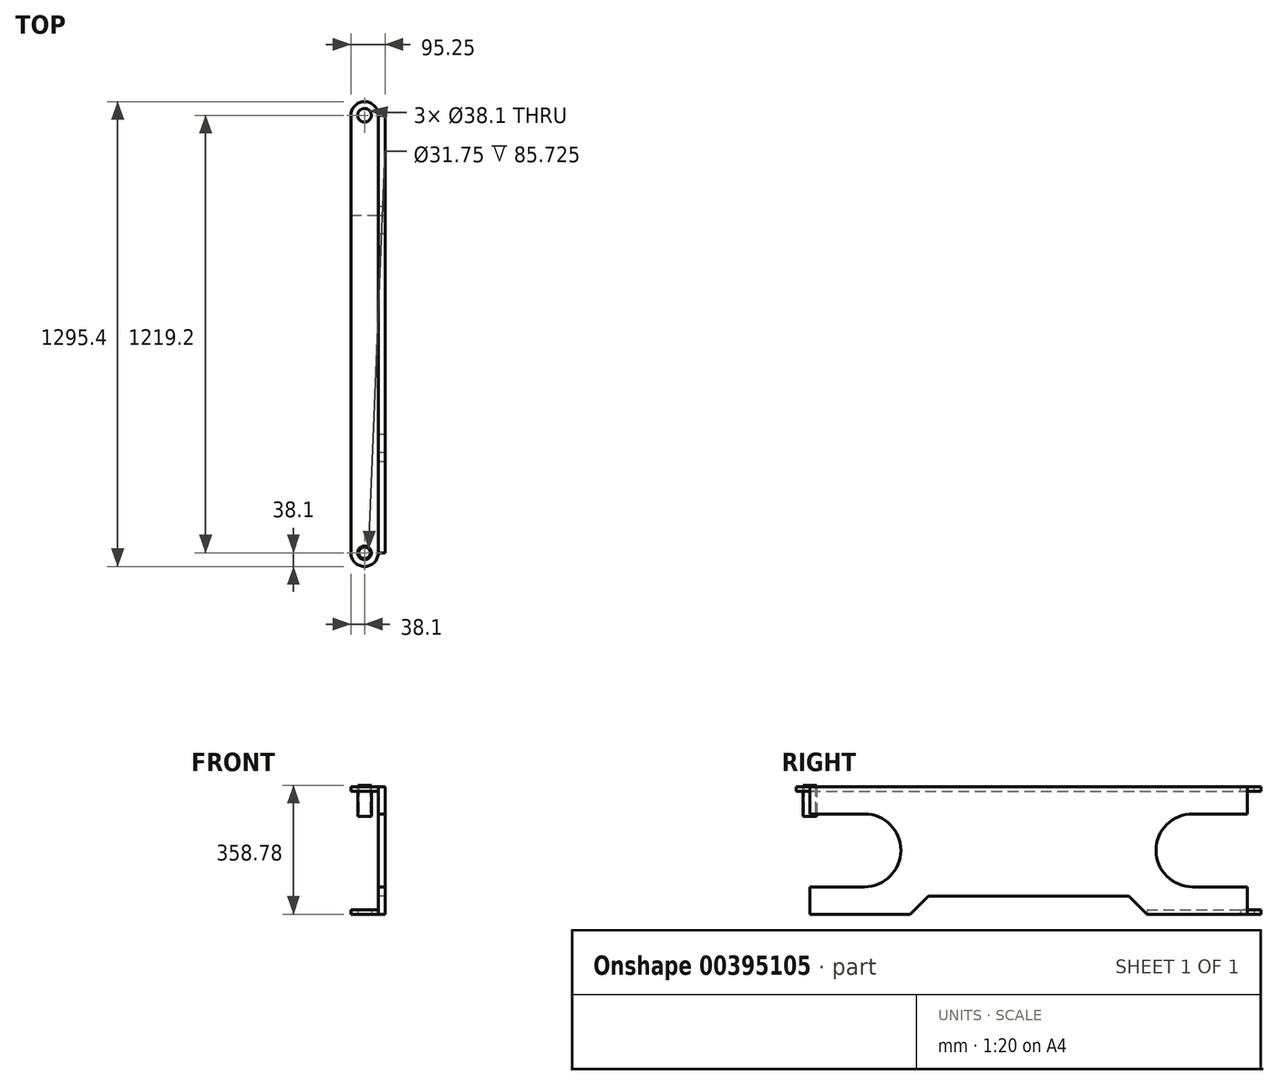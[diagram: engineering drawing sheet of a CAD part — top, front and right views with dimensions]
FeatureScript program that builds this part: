
annotation { "Feature Type Name" : "Feature", "Feature Type Description" : "" }
export const myFeature = defineFeature(function(context is Context, id is Id, definition is map)
    precondition{}
    {
        {
            var Q0;
            Q0=qCreatedBy(makeId("Right.planeOp"),FACE);
            var sketch = newSketch(context, id + "F0", { "sketchPlane" : qUnion([Q0])});
            skLineSegment(sketch, "E0.bottom", {"start": v(-609.6, 177.8) * mm, "end": v(609.6, 177.8) * mm});
            skLineSegment(sketch, "E0.top", {"start": v(-609.6, -177.8) * mm, "end": v(-330.2, -177.8) * mm});
            skLineSegment(sketch, "E0.left", {"start": v(-609.6, 177.8) * mm, "end": v(-609.6, 101.6) * mm});
            skLineSegment(sketch, "E0.right", {"start": v(609.6, 177.8) * mm, "end": v(609.6, 101.6) * mm});
            skPoint(sketch, "E0.middle", {"position": v(0, 0) * mm});
            skLineSegment(sketch, "E1", {"start": v(-609.6, 0) * mm, "end": v(609.6, 0) * mm, "construction": true});
            skLineSegment(sketch, "E2", {"start": v(0, 177.8) * mm, "end": v(0, -177.8) * mm, "construction": true});
            skArc(sketch, "E3", {"start": v(-457.2, -101.6) * mm, "mid": v(-355.6, 0) * mm, "end": v(-457.2, 101.6) * mm});
            skLineSegment(sketch, "E4", {"start": v(-457.2, 101.6) * mm, "end": v(-609.6, 101.6) * mm});
            skLineSegment(sketch, "E5", {"start": v(-457.2, -101.6) * mm, "end": v(-609.6, -101.6) * mm});
            skLineSegment(sketch, "E6.trimOffspring", {"start": v(-609.6, -101.6) * mm, "end": v(-609.6, -177.8) * mm});
            skLineSegment(sketch, "E7.MirrorCS", {"start": v(457.2, 101.6) * mm, "end": v(609.6, 101.6) * mm});
            skArc(sketch, "E8.MirrorCS", {"start": v(457.2, -101.6) * mm, "mid": v(355.6, 0) * mm, "end": v(457.2, 101.6) * mm});
            skLineSegment(sketch, "E9.MirrorCS", {"start": v(457.2, -101.6) * mm, "end": v(609.6, -101.6) * mm});
            skLineSegment(sketch, "E10.trimOffspring", {"start": v(609.6, -101.6) * mm, "end": v(609.6, -177.8) * mm});
            skLineSegment(sketch, "E11", {"start": v(-279.4, -127) * mm, "end": v(279.4, -127) * mm});
            skPoint(sketch, "E12", {"position": v(0, -127) * mm});
            skLineSegment(sketch, "E13", {"start": v(-279.4, -127) * mm, "end": v(-330.2, -177.8) * mm});
            skLineSegment(sketch, "E14", {"start": v(279.4, -127) * mm, "end": v(330.2, -177.8) * mm});
            skLineSegment(sketch, "E15.trimOffspring", {"start": v(330.2, -177.8) * mm, "end": v(609.6, -177.8) * mm});
            skSolve(sketch);
        }
        {
            var Q0;
            Q0 = qSketchRegion(id + "F0", true);
            extrude(context, id + "F1", {"entities" : qUnion([Q0]), "depth" : 19.05 * mm});
        }
        {
            var Q0;
            Q0=makeQuery(id+"F1.opExtrude","SWEPT_FACE",FACE,{"disambiguationData":[OSD([sQuery(id+"F0.wireOp",EDGE,"E0.bottom")])]});
            var sketch = newSketch(context, id + "F2", { "sketchPlane" : qUnion([Q0])});
            skLineSegment(sketch, "E16.0", {"start": v(0, -609.6) * mm, "end": v(0, 609.6) * mm});
            skLineSegment(sketch, "E17.0", {"start": v(-76.2, -609.6) * mm, "end": v(-76.2, 609.6) * mm});
            skLineSegment(sketch, "E18", {"start": v(0, -609.6) * mm, "end": v(-76.2, -609.6) * mm, "construction": true});
            skLineSegment(sketch, "E19", {"start": v(0, 609.6) * mm, "end": v(-76.2, 609.6) * mm, "construction": true});
            skArc(sketch, "E20", {"start": v(-76.2, -609.6) * mm, "mid": v(-38.1, -647.7) * mm, "end": v(0, -609.6) * mm});
            skArc(sketch, "E21", {"start": v(0, 609.6) * mm, "mid": v(-38.1, 647.7) * mm, "end": v(-76.2, 609.6) * mm});
            skCircle(sketch, "E22", {"center": v(-38.1, -609.6) * mm, "radius": 19.05 * mm});
            skCircle(sketch, "E23", {"center": v(-38.1, 609.6) * mm, "radius": 19.05 * mm});
            skSolve(sketch);
        }
        {
            var Q0;
            Q0 = qSketchRegion(id + "F2", true);
            extrude(context, id + "F3", {"entities" : qUnion([Q0]), "oppositeDirection" : true, "depth" : 12.7 * mm});
        }
        {
            var Q0;
            Q0=makeQuery(id+"F1.opExtrude","SWEPT_FACE",FACE,{"disambiguationData":[OSD([sQuery(id+"F0.wireOp",EDGE,"E15.trimOffspring")])]});
            var sketch = newSketch(context, id + "F4", { "sketchPlane" : qUnion([Q0])});
            skLineSegment(sketch, "E24.0", {"start": v(0, -330.2) * mm, "end": v(0, -609.6) * mm});
            skLineSegment(sketch, "E25.0", {"start": v(-76.2, -330.2) * mm, "end": v(-76.2, -609.6) * mm});
            skLineSegment(sketch, "E26", {"start": v(0, -609.6) * mm, "end": v(-76.2, -609.6) * mm, "construction": true});
            skLineSegment(sketch, "E27", {"start": v(0, -330.2) * mm, "end": v(-76.2, -330.2) * mm});
            skArc(sketch, "E28", {"start": v(-76.2, -609.6) * mm, "mid": v(-38.1, -647.7) * mm, "end": v(0, -609.6) * mm});
            skCircle(sketch, "E29", {"center": v(-38.1, -609.6) * mm, "radius": 19.05 * mm});
            skSolve(sketch);
        }
        {
            var Q0;
            Q0 = qSketchRegion(id + "F4", true);
            extrude(context, id + "F5", {"entities" : qUnion([Q0]), "oppositeDirection" : true, "depth" : 12.7 * mm});
        }
        {
            var Q0;
            Q0=makeQuery(id+"F2.imprint","IMPRINT",FACE,{"disambiguationData":[TD([[makeQuery(id+"F2.imprint","IMPRINT",EDGE,{"derivedFrom":sQuery(id+"F2.wireOp",EDGE,"E16.0")}),1.0]])]});
            var sketch = newSketch(context, id + "F6", { "sketchPlane" : qUnion([Q0])});
            skCircle(sketch, "E30.0", {"center": v(-38.1, -609.6) * mm, "radius": 19.05 * mm});
            skCircle(sketch, "E31.0", {"center": v(-38.1, -609.6) * mm, "radius": 15.88 * mm});
            skSolve(sketch);
        }
        {
            var Q0;
            Q0 = qSketchRegion(id + "F6", true);
            extrude(context, id + "F7", {"entities" : qUnion([Q0]), "depth" : 3.17 * mm, "hasSecondDirection" : true, "secondDirectionOppositeDirection" : true, "secondDirectionDepth" : 82.55 * mm});
        }
    });
